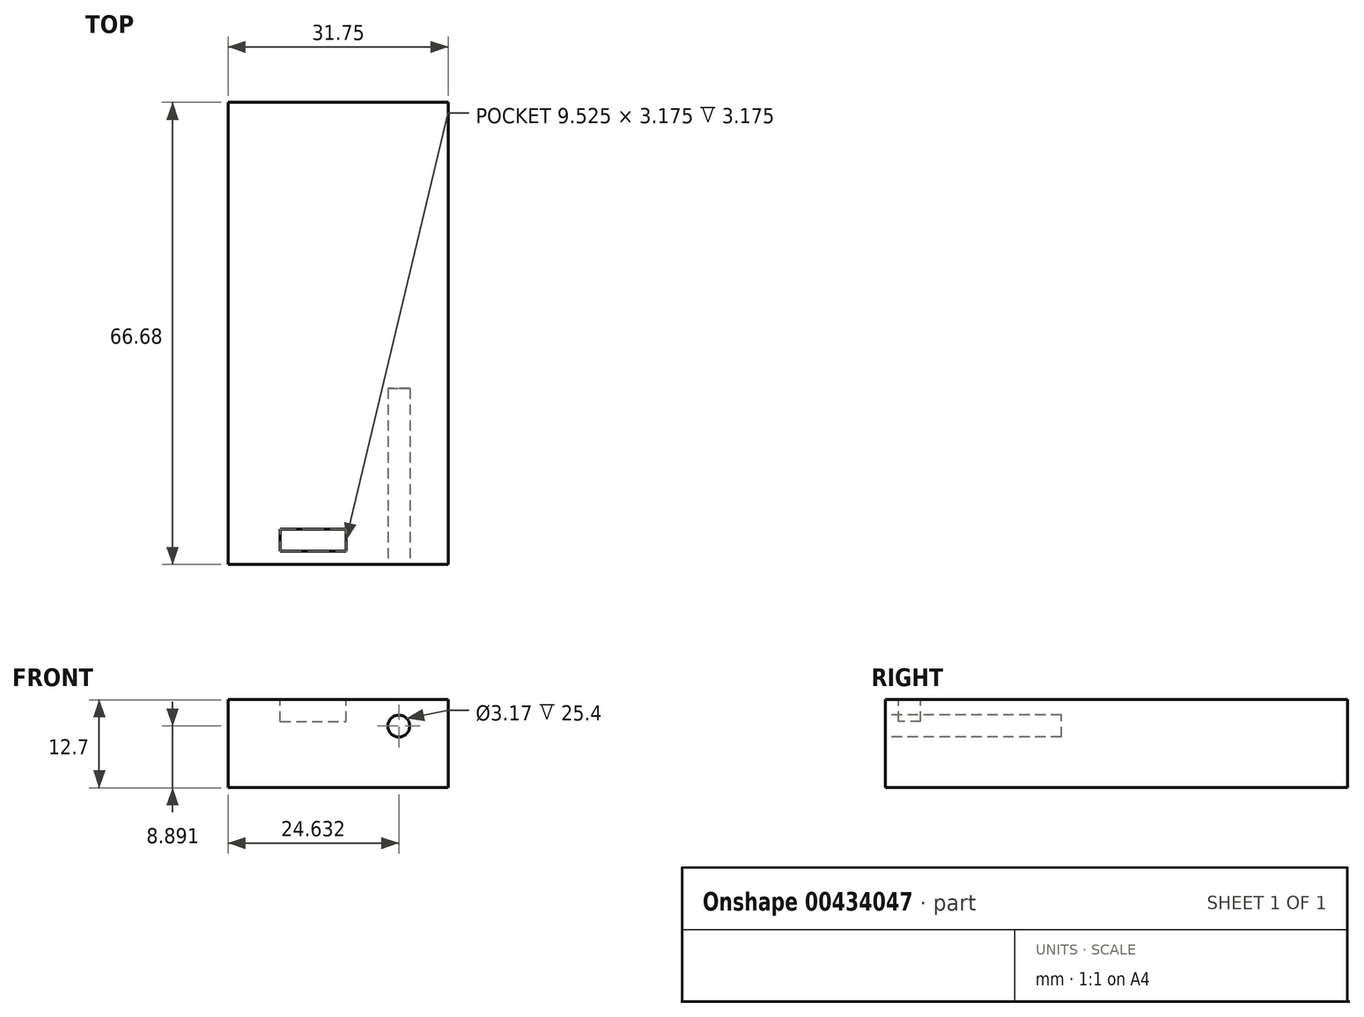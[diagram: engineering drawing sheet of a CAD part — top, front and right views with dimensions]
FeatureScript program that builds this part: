
annotation { "Feature Type Name" : "Feature", "Feature Type Description" : "" }
export const myFeature = defineFeature(function(context is Context, id is Id, definition is map)
    precondition{}
    {
        {
            var Q0;
            Q0=qCreatedBy(makeId("Front.planeOp"),FACE);
            var sketch = newSketch(context, id + "F0", { "sketchPlane" : qUnion([Q0])});
            skLineSegment(sketch, "E0.bottom", {"start": v(-112.66, -6) * mm, "end": v(-80.91, -6) * mm});
            skLineSegment(sketch, "E0.top", {"start": v(-112.66, -18.7) * mm, "end": v(-80.91, -18.7) * mm});
            skLineSegment(sketch, "E0.left", {"start": v(-112.66, -6) * mm, "end": v(-112.66, -18.7) * mm});
            skLineSegment(sketch, "E0.right", {"start": v(-80.91, -6) * mm, "end": v(-80.91, -18.7) * mm});
            skSolve(sketch);
        }
        {
            var Q0;
            Q0=makeQuery(id+"F0.imprint","IMPRINT",FACE,{"disambiguationData":[TD([[makeQuery(id+"F0.imprint","IMPRINT",EDGE,{"derivedFrom":sQuery(id+"F0.wireOp",EDGE,"E0.bottom")}),-1.0]])]});
            extrude(context, id + "F1", {"entities" : qUnion([Q0]), "depth" : 66.67 * mm});
        }
        {
            var Q0;
            Q0=makeQuery(id+"F1.opExtrude","CAP_FACE",FACE,{"disambiguationData":[OSD([sQuery(id+"F0.wireOp",EDGE,"E0.bottom"),sQuery(id+"F0.wireOp",EDGE,"E0.top"),sQuery(id+"F0.wireOp",EDGE,"E0.left"),sQuery(id+"F0.wireOp",EDGE,"E0.right")])],"isStart":false});
            var sketch = newSketch(context, id + "F2", { "sketchPlane" : qUnion([Q0])});
            skCircle(sketch, "E1", {"center": v(-88.03, -9.82) * mm, "radius": 1.59 * mm});
            skSolve(sketch);
        }
        {
            var Q0;
            Q0=makeQuery(id+"F2.imprint","IMPRINT",FACE,{"disambiguationData":[TD([[makeQuery(id+"F2.imprint","IMPRINT",EDGE,{"derivedFrom":sQuery(id+"F2.wireOp",EDGE,"E1")}),1.0]])]});
            extrude(context, id + "F3", {"entities" : qUnion([Q0]), "operationType" : NewBodyOperationType.REMOVE, "oppositeDirection" : true, "depth" : 25.4 * mm});
        }
        {
            var Q0;
            Q0=makeQuery(id+"F1.opExtrude","SWEPT_FACE",FACE,{"disambiguationData":[OSD([sQuery(id+"F0.wireOp",EDGE,"E0.bottom")])]});
            var sketch = newSketch(context, id + "F4", { "sketchPlane" : qUnion([Q0])});
            skLineSegment(sketch, "E2.bottom", {"start": v(-105.12, -61.57) * mm, "end": v(-95.6, -61.57) * mm});
            skLineSegment(sketch, "E2.top", {"start": v(-105.12, -64.75) * mm, "end": v(-95.6, -64.75) * mm});
            skLineSegment(sketch, "E2.left", {"start": v(-105.12, -61.57) * mm, "end": v(-105.12, -64.75) * mm});
            skLineSegment(sketch, "E2.right", {"start": v(-95.6, -61.57) * mm, "end": v(-95.6, -64.75) * mm});
            skSolve(sketch);
        }
        {
            var Q0;
            Q0=makeQuery(id+"F4.imprint","IMPRINT",FACE,{"disambiguationData":[TD([[makeQuery(id+"F4.imprint","IMPRINT",EDGE,{"derivedFrom":sQuery(id+"F4.wireOp",EDGE,"E2.bottom")}),-1.0]])]});
            extrude(context, id + "F5", {"entities" : qUnion([Q0]), "operationType" : NewBodyOperationType.REMOVE, "oppositeDirection" : true, "depth" : 3.17 * mm});
        }
    });
